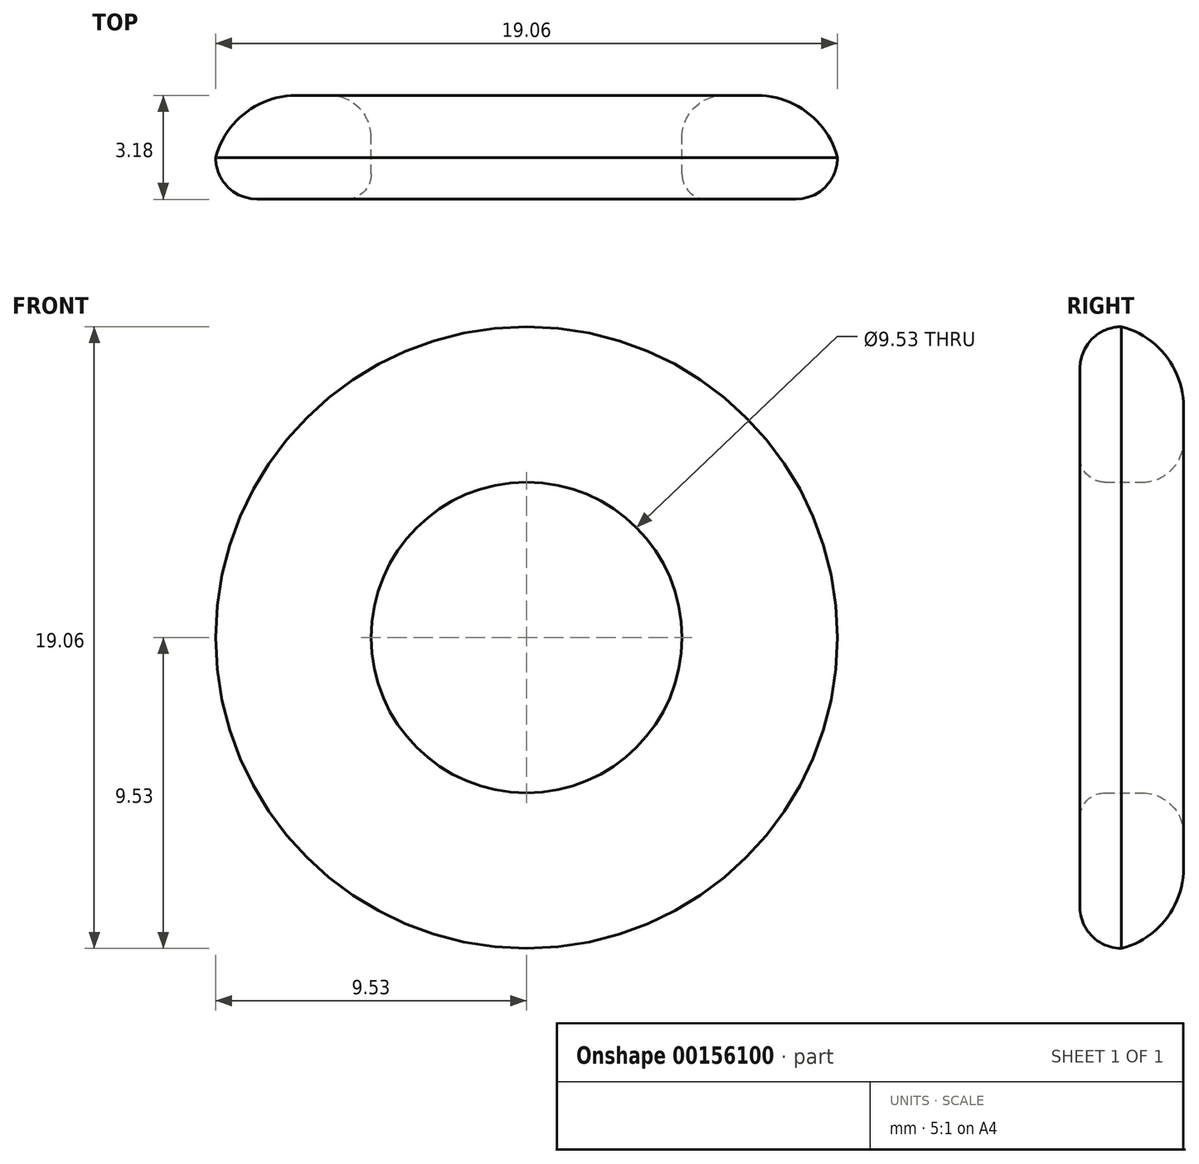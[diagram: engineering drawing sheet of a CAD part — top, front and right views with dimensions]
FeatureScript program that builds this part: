
annotation { "Feature Type Name" : "Feature", "Feature Type Description" : "" }
export const myFeature = defineFeature(function(context is Context, id is Id, definition is map)
    precondition{}
    {
        {
            var Q0;
            Q0=qCreatedBy(makeId("Front.planeOp"),FACE);
            var sketch = newSketch(context, id + "F0", { "sketchPlane" : qUnion([Q0])});
            skCircle(sketch, "E0", {"center": v(0, 0) * mm, "radius": 9.53 * mm});
            skCircle(sketch, "E1", {"center": v(0, 0) * mm, "radius": 4.76 * mm});
            skSolve(sketch);
        }
        {
            var Q0;
            Q0 = qSketchRegion(id + "F0", true);
            extrude(context, id + "F1", {"entities" : qUnion([Q0]), "depth" : 3.17 * mm});
        }
        {
            var Q0;
            Q0=makeQuery(id+"F1.opExtrude","CAP_EDGE",EDGE,{"disambiguationData":[OSD([sQuery(id+"F0.wireOp",EDGE,"E0")])],"isStart":false});
            fillet(context, id + "F2", {"entities" : qUnion([Q0]), "radius" : 1.27 * mm, "tangentPropagation" : true, "allowEdgeOverflow" : false});
        }
        {
            var Q0;
            Q0=makeQuery(id+"F1.opExtrude","CAP_EDGE",EDGE,{"disambiguationData":[OSD([sQuery(id+"F0.wireOp",EDGE,"E0")])],"isStart":true});
            fillet(context, id + "F3", {"entities" : qUnion([Q0]), "radius" : 2.54 * mm, "tangentPropagation" : true, "allowEdgeOverflow" : false});
        }
        {
            var Q0;
            Q0=makeQuery(id+"F1.opExtrude","CAP_EDGE",EDGE,{"disambiguationData":[OSD([sQuery(id+"F0.wireOp",EDGE,"E1")])],"isStart":true});
            fillet(context, id + "F4", {"entities" : qUnion([Q0]), "radius" : 1.27 * mm, "tangentPropagation" : true, "allowEdgeOverflow" : false});
        }
        {
            var Q0;
            Q0=makeQuery(id+"F1.opExtrude","CAP_EDGE",EDGE,{"disambiguationData":[OSD([sQuery(id+"F0.wireOp",EDGE,"E1")])],"isStart":false});
            fillet(context, id + "F5", {"entities" : qUnion([Q0]), "radius" : 0.76 * mm, "tangentPropagation" : true, "allowEdgeOverflow" : false});
        }
    });
